# Revit family: Faucet-Lavatory-KOHLER-JULY-K-29928IN
name_source: partatom
category: Plumbing Fixtures
units: mm (PartAtom-declared; Revit-internal decimal feet)

## family parameters
Cut with Voids When Loaded = No
Host = Face
OmniClass Number = 23.31.11.00
Part Type = Normal
Room Calculation Point = No
Round Connector Dimension = Use Diameter
Shared = No

## types (4) — shared parameters
ADA Compliant = No
Assembly Code = D2010
CW Connection = Yes
Cold Water Inlet = Cold Water Inlet
Date Modified = 09/17/2024
Default Elevation = 36"
HW Connection = Yes
Handle Clearance = 4 1/16"
Height = 5 1/2"
Hot Water Inlet = Hot Water Inlet
Length = 4 3/16"
Manufacturer = Kohler Co.
Master Format 2014 = 22 41 39
Master Format 2014 Name = Residential Faucets, Supplies, and Trim
Material = Brass Construction
Pressure = 43.51 psi
Product Name = JULY
Product Page URL = https://www.kohler.co.in
Spout Reach = 4 3/16"
URL = https://www.kohler.co.in
Vent Connection = No
Waste Connection = No
Waste Water Outlet = Waste Water Outlet
WaterSense Certified = No
Width = 1 7/8"

## per-type parameters (varying)
| type | 4 | Description | Drain Included | Finish | Flow Rate | Model | Type |
| CP-Polished Chrome | Yes | COMFORT HEIGHT Single Control LAV With DRAIN | Yes | Kohler-Metal-CP-Polished_Chrome | 6 GPM | K-29928IN-4-CP | 1 |
| 4ND, AF-Vibrant French Gold | No | Comfort Height Single Control Lav Without Drain | No | Kohler-Metal-AF-Vibrant_French_Gold | 10 GPM | K-29928IN-4ND-AF | 2 |
| 4ND, BN-Vibrant Brushed Nickel | No | Comfort Height Single Control Lav Without Drain | No | Kohler-Metal-BN-Vibrant_Brushed_Nickel | 10 GPM | K-29928IN-4ND-BN | 3 |
| 4ND, CP-Polished Chrome | No | Comfort Height Single Control Lav Without Drain | No | Kohler-Metal-CP-Polished_Chrome | 10 GPM | K-29928IN-4ND-CP | 4 |

## geometry (parser evidence)
native form markers: Sweep x5
no freeform markers — native parametric forms only
